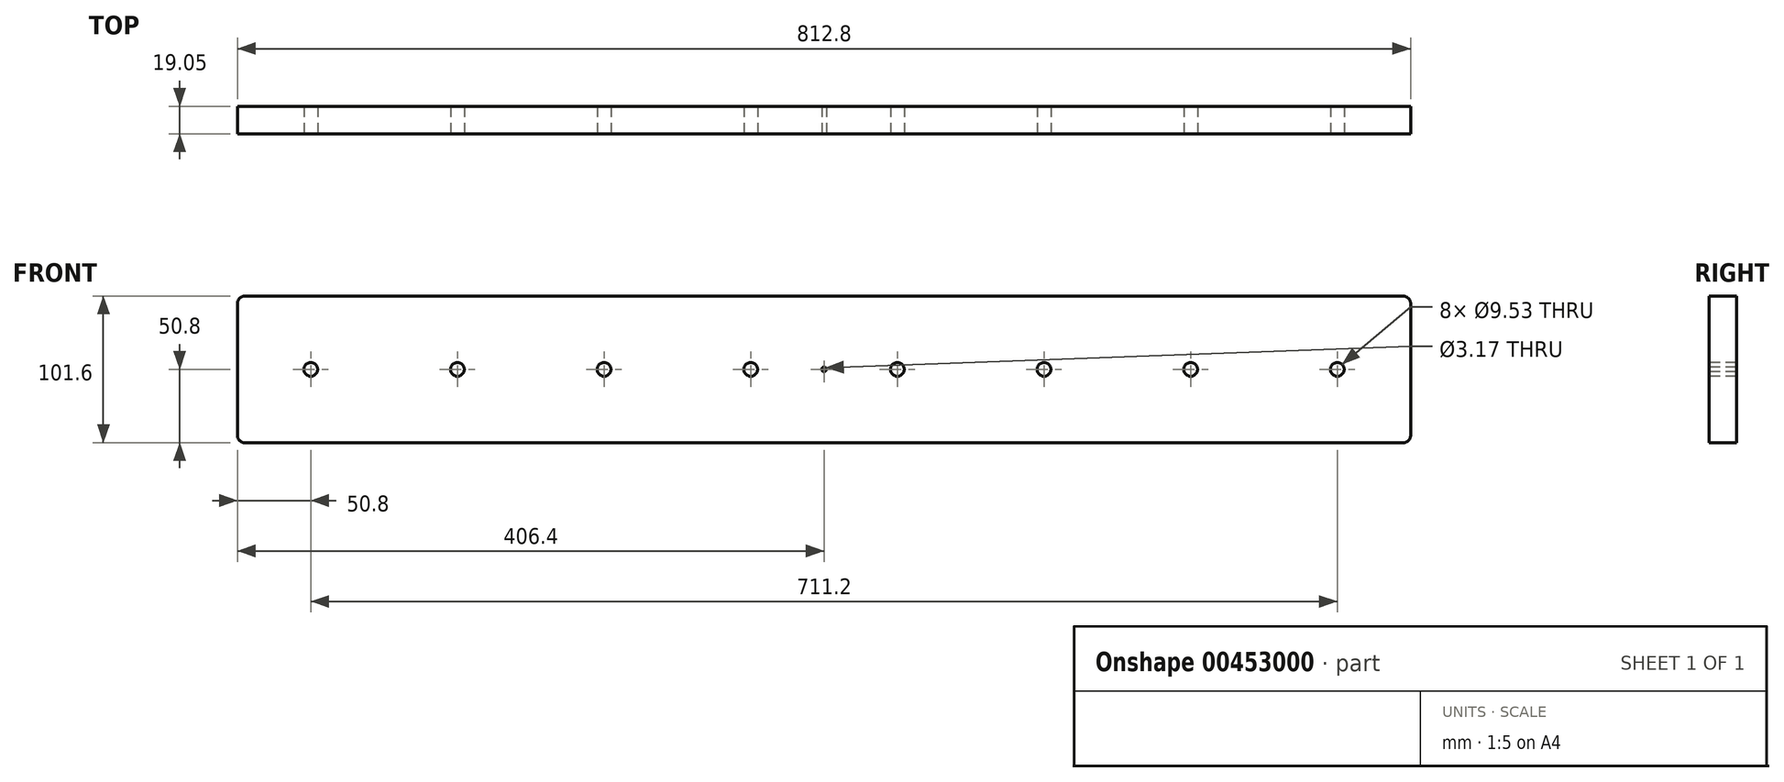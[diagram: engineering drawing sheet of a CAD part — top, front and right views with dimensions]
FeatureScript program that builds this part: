
annotation { "Feature Type Name" : "Feature", "Feature Type Description" : "" }
export const myFeature = defineFeature(function(context is Context, id is Id, definition is map)
    precondition{}
    {
        {
            var Q0;
            Q0=qCreatedBy(makeId("Front.planeOp"),FACE);
            var sketch = newSketch(context, id + "F0", { "sketchPlane" : qUnion([Q0])});
            skLineSegment(sketch, "E0.bottom", {"start": v(406.4, -50.8) * mm, "end": v(-406.4, -50.8) * mm});
            skLineSegment(sketch, "E0.top", {"start": v(406.4, 50.8) * mm, "end": v(-406.4, 50.8) * mm});
            skLineSegment(sketch, "E0.left", {"start": v(406.4, -50.8) * mm, "end": v(406.4, 50.8) * mm});
            skLineSegment(sketch, "E0.right", {"start": v(-406.4, -50.8) * mm, "end": v(-406.4, 50.8) * mm});
            skPoint(sketch, "E0.middle", {"position": v(0, 0) * mm});
            skPoint(sketch, "E1", {"position": v(-355.6, 0) * mm});
            skPoint(sketch, "E2", {"position": v(-254, 0) * mm});
            skPoint(sketch, "E3", {"position": v(-152.4, 0) * mm});
            skPoint(sketch, "E4", {"position": v(-50.8, 0) * mm});
            skPoint(sketch, "E5.MirrorP", {"position": v(50.8, 0) * mm});
            skPoint(sketch, "E6.MirrorP", {"position": v(152.4, 0) * mm});
            skPoint(sketch, "E7.MirrorP", {"position": v(254, 0) * mm});
            skPoint(sketch, "E8.MirrorP", {"position": v(355.6, 0) * mm});
            skSolve(sketch);
        }
        {
            var Q0;
            Q0=makeQuery(id+"F0.imprint","IMPRINT",FACE,{"disambiguationData":[TD([[makeQuery(id+"F0.imprint","IMPRINT",EDGE,{"derivedFrom":sQuery(id+"F0.wireOp",EDGE,"E0.bottom")}),-1.0]])]});
            extrude(context, id + "F1", {"entities" : qUnion([Q0]), "depth" : 19.05 * mm});
        }
        {
            var Q0;
            Q0=sQuery(id+"F0.wireOp",VERTEX,"E1");
            var Q1;
            Q1=sQuery(id+"F0.wireOp",VERTEX,"E2");
            var Q2;
            Q2=sQuery(id+"F0.wireOp",VERTEX,"E3");
            var Q3;
            Q3=sQuery(id+"F0.wireOp",VERTEX,"E4");
            var Q4;
            Q4=sQuery(id+"F0.wireOp",VERTEX,"E5.MirrorP");
            var Q5;
            Q5=sQuery(id+"F0.wireOp",VERTEX,"E6.MirrorP");
            var Q6;
            Q6=sQuery(id+"F0.wireOp",VERTEX,"E7.MirrorP");
            var Q7;
            Q7=sQuery(id+"F0.wireOp",VERTEX,"E8.MirrorP");
            var Q8;
            Q8=makeQuery(id+"F1.opExtrude","SWEPT_BODY",BODY,{"disambiguationData":[OSD([sQuery(id+"F0.wireOp",EDGE,"E0.bottom"),sQuery(id+"F0.wireOp",EDGE,"E0.top"),sQuery(id+"F0.wireOp",EDGE,"E0.left"),sQuery(id+"F0.wireOp",EDGE,"E0.right")])]});
            hole(context, id + "F2", {"style" : HoleStyle.SIMPLE, "endStyle" : HoleEndStyle.THROUGH, "oppositeDirection" : true, "holeDiameter" : 9.52 * mm, "isTappedThrough" : true, "tappedDepth" : 12.7 * mm, "tapClearance" : 3, "locations" : qUnion([Q0, Q1, Q2, Q3, Q4, Q5, Q6, Q7]), "scope" : qUnion([Q8]), "startStyle" : HoleStartStyle.PART});
        }
        {
            var Q0;
            Q0=sQuery(id+"F0.wireOp",VERTEX,"E0.middle");
            var Q1;
            Q1=makeQuery(id+"F1.opExtrude","SWEPT_BODY",BODY,{"disambiguationData":[OSD([sQuery(id+"F0.wireOp",EDGE,"E0.bottom"),sQuery(id+"F0.wireOp",EDGE,"E0.top"),sQuery(id+"F0.wireOp",EDGE,"E0.left"),sQuery(id+"F0.wireOp",EDGE,"E0.right")])]});
            hole(context, id + "F3", {"style" : HoleStyle.SIMPLE, "endStyle" : HoleEndStyle.THROUGH, "oppositeDirection" : true, "holeDiameter" : 3.17 * mm, "isTappedThrough" : true, "tappedDepth" : 12.7 * mm, "tapClearance" : 3, "locations" : qUnion([Q0]), "scope" : qUnion([Q1]), "startStyle" : HoleStartStyle.PART});
        }
        {
            var Q0;
            Q0=makeQuery(id+"F1.opExtrude","SWEPT_EDGE",EDGE,{"disambiguationData":[OSD([sQuery(id+"F0.wireOp",EDGE,"E0.top"),sQuery(id+"F0.wireOp",EDGE,"E0.right")])]});
            var Q1;
            Q1=makeQuery(id+"F1.opExtrude","SWEPT_EDGE",EDGE,{"disambiguationData":[OSD([sQuery(id+"F0.wireOp",EDGE,"E0.bottom"),sQuery(id+"F0.wireOp",EDGE,"E0.right")])]});
            var Q2;
            Q2=makeQuery(id+"F1.opExtrude","SWEPT_EDGE",EDGE,{"disambiguationData":[OSD([sQuery(id+"F0.wireOp",EDGE,"E0.top"),sQuery(id+"F0.wireOp",EDGE,"E0.left")])]});
            var Q3;
            Q3=makeQuery(id+"F1.opExtrude","SWEPT_EDGE",EDGE,{"disambiguationData":[OSD([sQuery(id+"F0.wireOp",EDGE,"E0.bottom"),sQuery(id+"F0.wireOp",EDGE,"E0.left")])]});
            fillet(context, id + "F4", {"entities" : qUnion([Q0, Q1, Q2, Q3]), "radius" : 5.08 * mm, "tangentPropagation" : true, "allowEdgeOverflow" : false});
        }
    });
